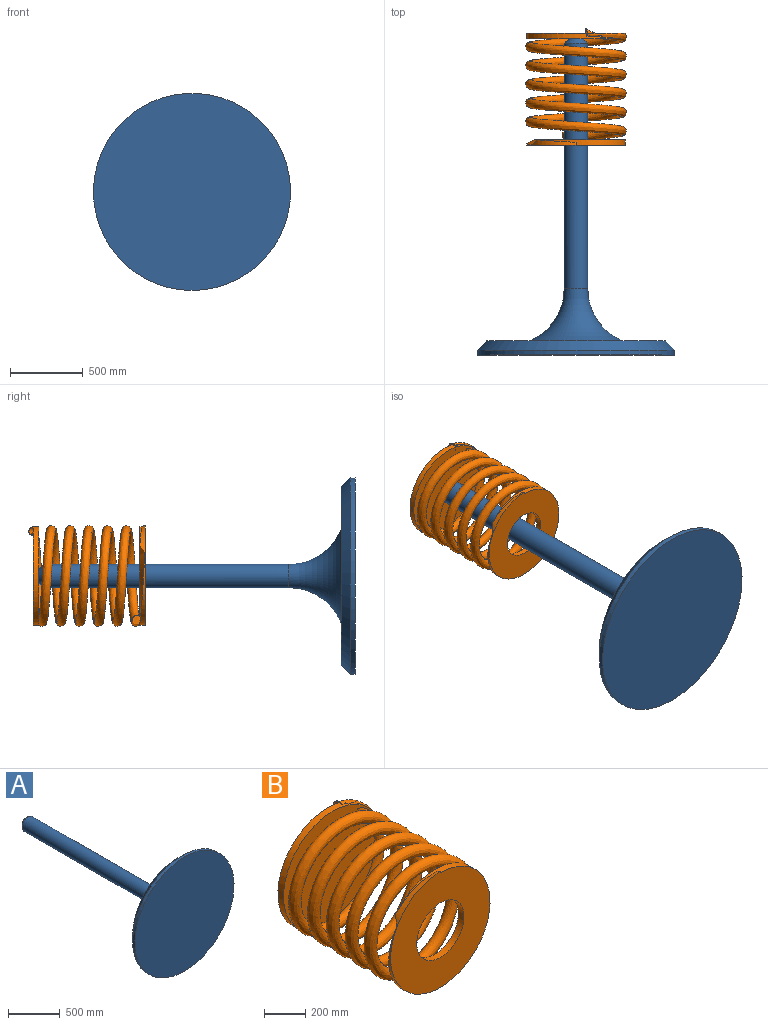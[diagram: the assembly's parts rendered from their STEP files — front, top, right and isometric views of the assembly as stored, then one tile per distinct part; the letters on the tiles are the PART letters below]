
ASSEMBLY  parts=2 mates=2
PART A: 7 faces, bbox 1608.7x2173x1608.7 mm
  f0: plane 1354.84x1354.84mm, normal (0,-1,0), area 1441661.6mm2, adj f1
  f1: cylinder r=677.42mm len=1354.84mm, axis (0,-1,0), area 137301.1mm2, adj f0,f2
  f2: cone r=677.42mm half-angle=45deg, axis (0,-1,0), area 369853.5mm2, adj f1,f3
  f3: torus R=468.12mm, axis (0,-1,0), area 1351661.9mm2, adj f2,f4
  f4: cylinder r=80.77mm len=1685.17mm, axis (0,-1,0), area 855233.3mm2, adj f3,f6
  f5: plane 98.04x98.04mm, normal (0,1,0), area 7549.7mm2, adj f6
  f6: cone r=80.77mm half-angle=45deg, axis (0,-1,0), area 18308.9mm2, adj f4,f5
PART B: 10 faces, bbox 693.7x833.5x693.9 mm
  f0: bspline ~831.29x692.05mm, area 4264077.2mm2, adj f1,f2,f3,f4,f5,f6,f7,f8
  f1: plane 62.23x60.69mm, normal (-0.98,0,0.22), area 2947.8mm2, adj f0,f3,f5
  f2: plane 19.64x6.99mm, normal (1,0,0), area 93.7mm2, adj f0,f7,f8
  f3: cylinder r=339.09mm len=678.18mm, axis (0,1,0), area 59645mm2, adj f0,f1,f4,f5
  f4: plane 678.18x644.54mm, normal (0,-1,0), area 322362.4mm2, adj f0,f3
  f5: plane 680.04x680.04mm, normal (0,1,0), area 362788.4mm2, adj f0,f1,f3
  f6: plane 678.18x623.53mm, normal (0,1,0), area 241647.4mm2, adj f0,f8,f9
  f7: plane 685.17x678.18mm, normal (0,-1,0), area 281061mm2, adj f0,f2,f8,f9
  f8: cylinder r=339.09mm len=678.18mm, axis (0,-1,0), area 59644.1mm2, adj f0,f2,f6,f7
  f9: cylinder r=161.29mm len=322.58mm, axis (0,-1,0), area 38611.1mm2, adj f6,f7
PLACE A t=(557.23,-719.47,925.87)mm
PLACE B t=(557.23,721.98,925.87)mm
MATE cylindrical A.f1 <-> B.f3  axis (0,-1,0) through (557.23,579.16,925.87)mm
MATE planar B.f4 <-> A.f1  axis (0,-1,0) through (529.94,1453.5,941.03)mm
